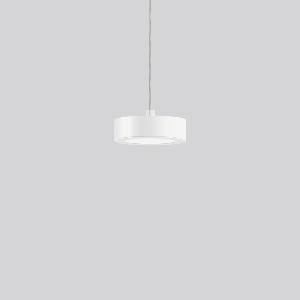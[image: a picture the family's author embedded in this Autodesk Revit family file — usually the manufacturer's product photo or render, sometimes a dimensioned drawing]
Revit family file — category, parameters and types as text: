
# Revit family: toledo_flat_round_p_901684_002_76_ebf0
name_source: partatom
category: Lighting Fixtures
units: mm (PartAtom-declared; Revit-internal decimal feet)

## family parameters
Cut with Voids When Loaded = No
Host = Face
Light Source = No
Part Type = Normal
Room Calculation Point = No
Round Connector Dimension = Use Diameter
Shared = No

## types (1)
- TOLEDO FLAT round P (1 x LED Modul 830, 780 lm, 3000)
    Apparent Load = 8 VA
    CIE Flux Codes = 47 79 96 100 100
    Color Rendering = 80
    Color Temperature = 3000
    Default Elevation = 1800 mm
    Description = Series: TOLEDO FLAT
Flat cylindrical pendant luminaire. Cylinder housing sheet steel, powder-coated. Housing: die cast aluminium and sheet steel, powder-coated. Bezel ring: die-cast aluminium, powder-coated. Canopy: sheet steel, powder-coated. Lightguide and diffuser made of non-yellowing plastic (PMMA) opal matt. Suitable for pendant. Transparent suspension cable 2 m, can be shortened. Mounting rings for retrofitting a fabric lampshade available as accessory. 
Colour: white
Diameter: 192 mm
Height: 83.3 mm
Suspension length: 2000 mm
Lamp: LED
Socket: without socket
Colour temperature: 3000K
Colour rendering index (CRI): 80
System power: 7.7 W
Rated luminous flux: 780 lm
Luminous efficiency: 101 lm/W
Control gear: Converter, dimmable, DALI
Protection class: I
Type of protection: IP 20
    Height = 83 mm
    Lamp = 1 x LED Modul 830
    Lamp Light Flux = 780 lm
    Lamp count = 1
    Length = 192 mm
    Lifetime = 50000 h
    Luminous efficacy = 101 lm/W
    Manufacturer = RZB
    ModVariant = No
    Model = 901684.002.76
    Mounting Place = Ceiling
    Mounting Type = Pendant
    Number of Poles = 1
    OnlyDefault = Yes
    Power Factor = 1
    Product Name = TOLEDO FLAT round P
    Product group = Pendant luminaires
    ProductGroupID = 902
    Protection Class = Protection class I
    Protection Degree = IP 20
    RLX_Detail_Level = 1
    RLX_Emergency_Light_Flux = 0 lm
    RLX_Emergency_Type = 0
    RLX_Emergency_Type_DB = No
    RlxData = <blob elided: 69165 chars, md5=3d9dc4cd>
    Socket = socket
    Standby Power = 0 W
    System Light Flux = 780 lm
    System Power = 8 W
    Type Comments = Product without accessories
    Type Image = 901684.002.jpg
    URL = http://relux.com
    VarID = ---
    Voltage = 230 V
    Voltage Range = 220-240 V
    Weight = 0.00 kg
    Width = 0 mm  [stored 0 ft]

note: [stored X ft] marks values corroborated as IEEE doubles in the binary element streams (Revit-internal decimal feet)

## geometry (parser evidence)
native form markers: Blend x4, Sweep x8
no freeform markers — native parametric forms only
